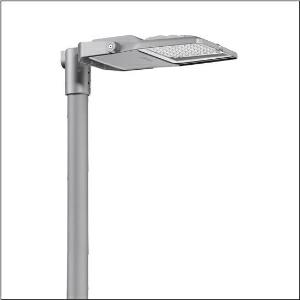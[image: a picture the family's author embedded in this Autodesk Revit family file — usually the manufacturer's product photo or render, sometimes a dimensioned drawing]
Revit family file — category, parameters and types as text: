
# Revit family: floodlight_fl_21_iq_mini___pl33t_5xa7772b2f3a_3cf2
name_source: partatom
category: Lighting Fixtures
units: mm (PartAtom-declared; Revit-internal decimal feet)

## family parameters
Cut with Voids When Loaded = No
Host = Face
Light Source = No
Part Type = Normal
Room Calculation Point = No
Round Connector Dimension = Use Diameter
Shared = No

## types (1)
- --- (1 x LED, 6170 lm, 45.5 W, 3000K)
    Apparent Load = 46 VA
    CIE Flux Codes = 26 75 99 100 100
    Color Rendering = 70
    Color Temperature = 3000K
    Default Elevation = 1800 mm
    Description = Floodlight FL 21 iQ mini, floodlight, primary light control with lens, of PMMA, primary optical cover: protective disc, of toughened safety glass, transparent, light distribution: PL33T, light emission: direct distribution, installation type: surface-mounted, LED, High Power LED, rated luminous flux: 6.170lm, luminous efficacy: 136lm/W, light colour: 730, colour temperature: 3000K, control: Auto-Match, Temp-Guard, Night-Set, Smart-Wire, Desk-Remote (wireless, voltage-free reading and setting of iQ features in the workshop via application-optimized NFC function/RFID function), optimised constant luminous flux control (CLO 2.0), Light-Fading, Lumen-Switch, with terminal, 6-pole, mains connection: 220..240V, AC, 50/60Hz, start of lifetime: 46W, end of service life: 48W, reduction: 22W, luminaire housing, of diecast aluminium, powder-coated, Siteco® metallic grey (DB 702S), corrosivity category C5 mid according to DIN EN ISO 12944, sealing non-destructively replaceable, please order mast flange separately, mast bracket, of steel, galvanised, powder-coated, protection rating (complete): IP66, insulation class (complete): insulation class II (safety insulation), certification: CE, ENEC, VDE, protection symbol: D, impact resistance: IK08, permissible operating ambient temperature: -40..+40°C, permissible operating ambient temperature for outdoor applications: -40..+50°C, standard: DIN EN 12944, LABS conformity tested according to VDMA 24364:2018-05, packaging unit: 1 piece

Light Distribution: PL33T
    Height = 70 mm
    Lamp = 1 x LED
    Lamp Light Flux = 6170 lm
    Lamp Power = 45.5 W
    Lamp count = 1
    Length = 485 mm
    Luminous efficacy = 136 lm/W
    Manufacturer = Siteco
    ModVariant = No
    Model = 5XA7772B2F3A
    Number of Poles = 1
    OnlyDefault = Yes
    Power Factor = 1
    Product Name = Floodlight FL 21 iQ mini | PL33T
    Product group = floodlight | pylon annexe
    ProductGroupID = 6200
    Protection Class = Protection class II
    Protection Degree = IP 66
    RLX_Detail_Level = 1
    RLX_Emergency_Light_Flux = 0 lm
    RLX_Emergency_Type = 0
    RLX_Emergency_Type_DB = No
    RlxData = <blob elided: 101041 chars, md5=5b732c9f>
    Socket = socket
    Standby Power = 0 W
    System Light Flux = 6170 lm
    System Power = 46 W
    Type Comments = factory setting: luminous flux: 100 % | dim-lin: 254 | 463 mA
    Type Image = l_1007125.jpg
    URL = http://relux.com
    VarID = @adj_082515
    Voltage = 0 V
    Weight = 0.00 kg
    Width = 337 mm

## geometry (parser evidence)
native form markers: Blend x4, Sweep x13
no freeform markers — native parametric forms only
